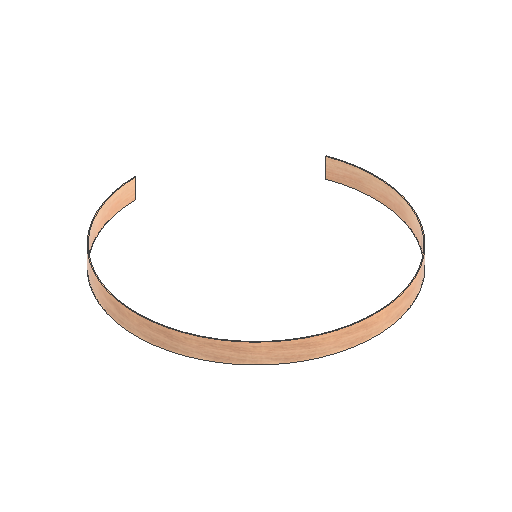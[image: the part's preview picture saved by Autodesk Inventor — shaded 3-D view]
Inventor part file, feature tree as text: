
AUTODESK INVENTOR PART (.ipt)
format: ipt  version: 2021 (Build 250183000, 183)  size: 124,928 bytes
history: native  units: mm
features: other x4, extrude x2, sketch x2, reference x2
ambient origin geometry x8: Origin, YZ Plane, XZ Plane, XY Plane, X Axis, Y Axis, Z Axis, Center Point
bodies: Solid1 (feature_tree)
feature tree (10):
  extrude  "Extrusion1"  Depth=1208.0mm
  extrude  "Extrusion2"  Depth=100.0mm TaperAngle=0.0deg
  sketch  "Sketch1"  dims[d0=1200.0mm d1=1208.0mm]
  sketch  "Sketch2"  dims[d2=100.0mm d3=0.0mm d4=100.0mm d5=0.0mm]
  reference  "Reference1"
  reference  "Reference2"
  other  "Full Scale Assembly.iam"
  other  "Support A Assembly Single LEFT:1"
  other  "Support A:1"
  other  "Support A Assembly Single RIGHT:1"
